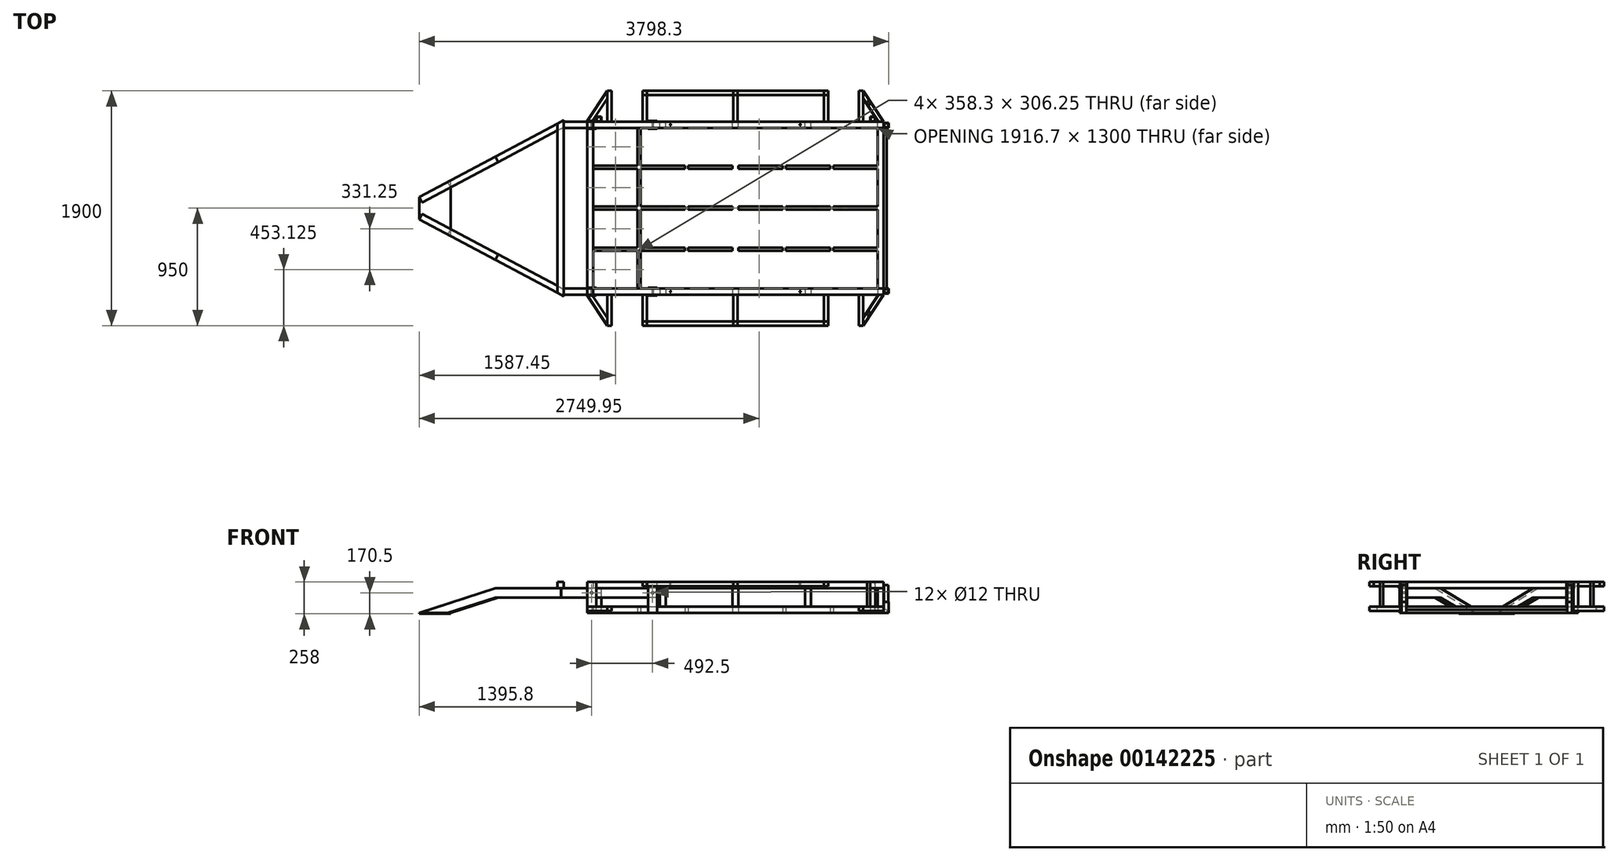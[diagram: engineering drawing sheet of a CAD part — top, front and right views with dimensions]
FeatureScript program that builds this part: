
annotation { "Feature Type Name" : "Feature", "Feature Type Description" : "" }
export const myFeature = defineFeature(function(context is Context, id is Id, definition is map)
    precondition{}
    {
        {
            var Q0;
            Q0=qCreatedBy(makeId("Top.planeOp"),FACE);
            var sketch = newSketch(context, id + "F0", { "sketchPlane" : qUnion([Q0])});
            skLineSegment(sketch, "E0.bottom", {"start": v(0, 700) * mm, "end": v(2400, 700) * mm});
            skLineSegment(sketch, "E0.top", {"start": v(0, -700) * mm, "end": v(2400, -700) * mm});
            skLineSegment(sketch, "E0.left", {"start": v(0, 700) * mm, "end": v(0, -700) * mm});
            skLineSegment(sketch, "E0.right", {"start": v(2400, 700) * mm, "end": v(2400, -700) * mm});
            skLineSegment(sketch, "E1.0", {"start": v(50, 650) * mm, "end": v(2350, 650) * mm});
            skLineSegment(sketch, "E2.0", {"start": v(50, -650) * mm, "end": v(2350, -650) * mm});
            skLineSegment(sketch, "E3.0", {"start": v(50, 650) * mm, "end": v(50, -650) * mm});
            skLineSegment(sketch, "E4", {"start": v(420.8, -898.2) * mm, "end": v(420.8, -1248.28) * mm, "construction": true});
            skLineSegment(sketch, "E5", {"start": v(804.2, -904.13) * mm, "end": v(804.2, -1242.34) * mm, "construction": true});
            skPoint(sketch, "E6.startSnap0", {"position": v(1200, -650) * mm});
            skLineSegment(sketch, "E7", {"start": v(1979.1, -862.6) * mm, "end": v(1979.1, -1218.6) * mm, "construction": true});
            skLineSegment(sketch, "E8", {"start": v(1595.8, -880.4) * mm, "end": v(1595.8, -1230.47) * mm, "construction": true});
            skLineSegment(sketch, "E9", {"start": v(1200, -876.97) * mm, "end": v(1200, -1568.23) * mm, "construction": true});
            skPoint(sketch, "E9.startSnap0", {"position": v(1200, -700) * mm});
            skLineSegment(sketch, "E10", {"start": v(408.3, 650) * mm, "end": v(408.3, -650) * mm});
            skLineSegment(sketch, "E11", {"start": v(791.7, -650) * mm, "end": v(791.7, 650) * mm});
            skLineSegment(sketch, "E12", {"start": v(1608.3, -650) * mm, "end": v(1608.3, 650) * mm});
            skLineSegment(sketch, "E13.0", {"start": v(1966.6, -650) * mm, "end": v(1966.6, 650) * mm});
            skLineSegment(sketch, "E14.0", {"start": v(1583.3, -650) * mm, "end": v(1583.3, 650) * mm});
            skLineSegment(sketch, "E15.0", {"start": v(816.7, -650) * mm, "end": v(816.7, 650) * mm});
            skLineSegment(sketch, "E16.0", {"start": v(433.3, 650) * mm, "end": v(433.3, -650) * mm});
            skLineSegment(sketch, "E17", {"start": v(-204.2, 331.25) * mm, "end": v(-574.65, 331.25) * mm, "construction": true});
            skLineSegment(sketch, "E18", {"start": v(-235.96, 0) * mm, "end": v(-549.96, 0) * mm});
            skLineSegment(sketch, "E19", {"start": v(-193.62, -331.25) * mm, "end": v(-624.05, -331.25) * mm, "construction": true});
            skLineSegment(sketch, "E20", {"start": v(50, 343.75) * mm, "end": v(408.3, 343.75) * mm});
            skLineSegment(sketch, "E21", {"start": v(50, -318.75) * mm, "end": v(408.3, -318.75) * mm});
            skLineSegment(sketch, "E22.0", {"start": v(50, 318.75) * mm, "end": v(408.3, 318.75) * mm});
            skLineSegment(sketch, "E23.0", {"start": v(50, -343.75) * mm, "end": v(408.3, -343.75) * mm});
            skLineSegment(sketch, "E24", {"start": v(50, 12.5) * mm, "end": v(408.3, 12.5) * mm});
            skLineSegment(sketch, "E25.0", {"start": v(50, -12.5) * mm, "end": v(408.3, -12.5) * mm});
            skLineSegment(sketch, "E26.trimOffspring", {"start": v(433.3, 343.75) * mm, "end": v(791.7, 343.75) * mm});
            skLineSegment(sketch, "E27.trimOffspring", {"start": v(433.3, 318.75) * mm, "end": v(791.7, 318.75) * mm});
            skLineSegment(sketch, "E28.trimOffspring", {"start": v(433.3, 12.5) * mm, "end": v(791.7, 12.5) * mm});
            skLineSegment(sketch, "E29.trimOffspring", {"start": v(433.3, -12.5) * mm, "end": v(791.7, -12.5) * mm});
            skLineSegment(sketch, "E30.trimOffspring", {"start": v(433.3, -318.75) * mm, "end": v(791.7, -318.75) * mm});
            skLineSegment(sketch, "E31.trimOffspring", {"start": v(433.3, -343.75) * mm, "end": v(791.7, -343.75) * mm});
            skLineSegment(sketch, "E32.trimOffspring", {"start": v(1608.3, -343.75) * mm, "end": v(1966.6, -343.75) * mm});
            skLineSegment(sketch, "E33.trimOffspring", {"start": v(1608.3, -318.75) * mm, "end": v(1966.6, -318.75) * mm});
            skLineSegment(sketch, "E34.trimOffspring", {"start": v(1608.3, -12.5) * mm, "end": v(1966.6, -12.5) * mm});
            skLineSegment(sketch, "E35.trimOffspring", {"start": v(1608.3, 12.5) * mm, "end": v(1966.6, 12.5) * mm});
            skLineSegment(sketch, "E36.trimOffspring", {"start": v(1608.3, 343.75) * mm, "end": v(1966.6, 343.75) * mm});
            skLineSegment(sketch, "E37.trimOffspring", {"start": v(1608.3, 318.75) * mm, "end": v(1966.6, 318.75) * mm});
            skLineSegment(sketch, "E38", {"start": v(1175, 650) * mm, "end": v(1175, -650) * mm});
            skLineSegment(sketch, "E39.0", {"start": v(1225, 650) * mm, "end": v(1225, -650) * mm});
            skLineSegment(sketch, "E40", {"start": v(1583.3, 343.75) * mm, "end": v(1225, 343.75) * mm});
            skLineSegment(sketch, "E41", {"start": v(1175, 343.75) * mm, "end": v(816.7, 343.75) * mm});
            skLineSegment(sketch, "E42", {"start": v(1175, 12.5) * mm, "end": v(816.7, 12.5) * mm});
            skLineSegment(sketch, "E43", {"start": v(1583.3, 12.5) * mm, "end": v(1225, 12.5) * mm});
            skLineSegment(sketch, "E44", {"start": v(1583.3, -318.75) * mm, "end": v(1225, -318.75) * mm});
            skLineSegment(sketch, "E45", {"start": v(1175, -318.75) * mm, "end": v(816.7, -318.75) * mm});
            skLineSegment(sketch, "E46.0", {"start": v(1175, 318.75) * mm, "end": v(816.7, 318.75) * mm});
            skLineSegment(sketch, "E47.0", {"start": v(1583.3, 318.75) * mm, "end": v(1225, 318.75) * mm});
            skLineSegment(sketch, "E48.0", {"start": v(1175, -12.5) * mm, "end": v(816.7, -12.5) * mm});
            skLineSegment(sketch, "E49.0", {"start": v(1583.3, -12.5) * mm, "end": v(1225, -12.5) * mm});
            skLineSegment(sketch, "E50.0", {"start": v(1175, -343.75) * mm, "end": v(816.7, -343.75) * mm});
            skLineSegment(sketch, "E51.0", {"start": v(1583.3, -343.75) * mm, "end": v(1225, -343.75) * mm});
            skLineSegment(sketch, "E52", {"start": v(816.7, 343.75) * mm, "end": v(816.7, 318.75) * mm});
            skLineSegment(sketch, "E53", {"start": v(1175, 343.75) * mm, "end": v(1175, 318.75) * mm});
            skLineSegment(sketch, "E54", {"start": v(1225, 343.75) * mm, "end": v(1225, 318.75) * mm});
            skLineSegment(sketch, "E55", {"start": v(1583.3, 343.75) * mm, "end": v(1583.3, 318.75) * mm});
            skLineSegment(sketch, "E56", {"start": v(1583.3, 12.5) * mm, "end": v(1583.3, -12.5) * mm});
            skLineSegment(sketch, "E57", {"start": v(1225, 12.5) * mm, "end": v(1225, -12.5) * mm});
            skLineSegment(sketch, "E58", {"start": v(1175, 12.5) * mm, "end": v(1175, -12.5) * mm});
            skLineSegment(sketch, "E59", {"start": v(816.7, 12.5) * mm, "end": v(816.7, -12.5) * mm});
            skLineSegment(sketch, "E60", {"start": v(1583.3, -318.75) * mm, "end": v(1583.3, -343.75) * mm});
            skLineSegment(sketch, "E61", {"start": v(1225, -318.75) * mm, "end": v(1225, -343.75) * mm});
            skLineSegment(sketch, "E62", {"start": v(1175, -318.75) * mm, "end": v(1175, -343.75) * mm});
            skLineSegment(sketch, "E63", {"start": v(816.7, -318.75) * mm, "end": v(816.7, -343.75) * mm});
            skLineSegment(sketch, "E64", {"start": v(2350, 650) * mm, "end": v(2350, -650) * mm});
            skLineSegment(sketch, "E65.0", {"start": v(1991.6, -650) * mm, "end": v(1991.6, 650) * mm});
            skLineSegment(sketch, "E66", {"start": v(1991.6, 343.75) * mm, "end": v(2350, 343.75) * mm});
            skLineSegment(sketch, "E67", {"start": v(1991.6, 12.5) * mm, "end": v(2350, 12.5) * mm});
            skLineSegment(sketch, "E68", {"start": v(1991.6, -318.75) * mm, "end": v(2350, -318.75) * mm});
            skLineSegment(sketch, "E69.0", {"start": v(1991.6, 318.75) * mm, "end": v(2350, 318.75) * mm});
            skLineSegment(sketch, "E70.0", {"start": v(1991.6, -12.5) * mm, "end": v(2350, -12.5) * mm});
            skLineSegment(sketch, "E71.0", {"start": v(1991.6, -343.75) * mm, "end": v(2350, -343.75) * mm});
            skLineSegment(sketch, "E72", {"start": v(1966.6, 650) * mm, "end": v(1991.6, 650) * mm});
            skLineSegment(sketch, "E73", {"start": v(1966.6, -650) * mm, "end": v(1991.6, -650) * mm});
            skLineSegment(sketch, "E74", {"start": v(1991.6, -343.75) * mm, "end": v(1991.6, -318.75) * mm});
            skLineSegment(sketch, "E75", {"start": v(2350, -343.75) * mm, "end": v(2350, -318.75) * mm});
            skLineSegment(sketch, "E76", {"start": v(2350, -12.5) * mm, "end": v(2350, 12.5) * mm});
            skLineSegment(sketch, "E77", {"start": v(1991.6, -12.5) * mm, "end": v(1991.6, 12.5) * mm});
            skLineSegment(sketch, "E78", {"start": v(2350, 318.75) * mm, "end": v(2350, 343.75) * mm});
            skLineSegment(sketch, "E79", {"start": v(1991.6, 318.75) * mm, "end": v(1991.6, 343.75) * mm});
            skLineSegment(sketch, "E80", {"start": v(2350, 343.75) * mm, "end": v(2350, 318.75) * mm});
            skLineSegment(sketch, "E81", {"start": v(2350, 12.5) * mm, "end": v(2350, -12.5) * mm});
            skLineSegment(sketch, "E82", {"start": v(2350, -318.75) * mm, "end": v(2350, -343.75) * mm});
            skLineSegment(sketch, "E83", {"start": v(1991.6, -318.75) * mm, "end": v(1991.6, -343.75) * mm});
            skLineSegment(sketch, "E84", {"start": v(1966.6, 343.75) * mm, "end": v(1966.6, 318.75) * mm});
            skLineSegment(sketch, "E85", {"start": v(1966.6, 12.5) * mm, "end": v(1966.6, -12.5) * mm});
            skLineSegment(sketch, "E86", {"start": v(1966.6, -318.75) * mm, "end": v(1966.6, -343.75) * mm});
            skLineSegment(sketch, "E87", {"start": v(1608.3, -318.75) * mm, "end": v(1608.3, -343.75) * mm});
            skLineSegment(sketch, "E88", {"start": v(1608.3, 12.5) * mm, "end": v(1608.3, -12.5) * mm});
            skLineSegment(sketch, "E89", {"start": v(1608.3, 343.75) * mm, "end": v(1608.3, 318.75) * mm});
            skSolve(sketch);
        }
        {
            var Q0;
            Q0=qSketchRegion(id+"F0",true);
            var Q1;
            Q1=makeQuery(id+"F0.imprint","IMPRINT",FACE,{"disambiguationData":[TD([[makeQuery(id+"F0.imprint","IMPRINT",EDGE,{"derivedFrom":sQuery(id+"F0.wireOp",EDGE,"E66")}),-1.0]])]});
            var Q2;
            {var subQ6=sQuery(id+"F0.wireOp",EDGE,"E72");Q2=makeQuery(id+"F0.imprint","IMPRINT",FACE,{"disambiguationData":[TD([[makeQuery(id+"F0.imprint","IMPRINT",EDGE,{"derivedFrom":subQ6}),-1.0]])]});}
            var Q3;
            Q3=makeQuery(id+"F0.imprint","IMPRINT",FACE,{"disambiguationData":[TD([[makeQuery(id+"F0.imprint","IMPRINT",EDGE,{"derivedFrom":sQuery(id+"F0.wireOp",EDGE,"E67")}),-1.0]])]});
            var Q4;
            Q4=makeQuery(id+"F0.imprint","IMPRINT",FACE,{"disambiguationData":[TD([[makeQuery(id+"F0.imprint","IMPRINT",EDGE,{"derivedFrom":sQuery(id+"F0.wireOp",EDGE,"E68")}),-1.0]])]});
            var Q5;
            {var subQ0=sQuery(id+"F0.wireOp",EDGE,"E32.trimOffspring");Q5=makeQuery(id+"F0.imprint","IMPRINT",FACE,{"disambiguationData":[TD([[makeQuery(id+"F0.imprint","IMPRINT",EDGE,{"derivedFrom":subQ0}),1.0]])]});}
            var Q6;
            {var subQ15=sQuery(id+"F0.wireOp",EDGE,"E55");Q6=makeQuery(id+"F0.imprint","IMPRINT",FACE,{"disambiguationData":[TD([[makeQuery(id+"F0.imprint","IMPRINT",EDGE,{"derivedFrom":subQ15}),1.0]])]});}
            var Q7;
            {var subQ0=sQuery(id+"F0.wireOp",EDGE,"E34.trimOffspring");Q7=makeQuery(id+"F0.imprint","IMPRINT",FACE,{"disambiguationData":[TD([[makeQuery(id+"F0.imprint","IMPRINT",EDGE,{"derivedFrom":subQ0}),1.0]])]});}
            var Q8;
            {var subQ0=sQuery(id+"F0.wireOp",EDGE,"E36.trimOffspring");Q8=makeQuery(id+"F0.imprint","IMPRINT",FACE,{"disambiguationData":[TD([[makeQuery(id+"F0.imprint","IMPRINT",EDGE,{"derivedFrom":subQ0}),-1.0]])]});}
            var Q9;
            {var subQ13=sQuery(id+"F0.wireOp",EDGE,"E53");Q9=makeQuery(id+"F0.imprint","IMPRINT",FACE,{"disambiguationData":[TD([[makeQuery(id+"F0.imprint","IMPRINT",EDGE,{"derivedFrom":subQ13}),1.0]])]});}
            var Q10;
            {var subQ16=sQuery(id+"F0.wireOp",EDGE,"E52");Q10=makeQuery(id+"F0.imprint","IMPRINT",FACE,{"disambiguationData":[TD([[makeQuery(id+"F0.imprint","IMPRINT",EDGE,{"derivedFrom":subQ16}),-1.0]])]});}
            var Q11;
            Q11=makeQuery(id+"F0.imprint","IMPRINT",FACE,{"disambiguationData":[TD([[makeQuery(id+"F0.imprint","IMPRINT",EDGE,{"derivedFrom":sQuery(id+"F0.wireOp",EDGE,"E45")}),1.0]])]});
            var Q12;
            Q12=makeQuery(id+"F0.imprint","IMPRINT",FACE,{"disambiguationData":[TD([[makeQuery(id+"F0.imprint","IMPRINT",EDGE,{"derivedFrom":sQuery(id+"F0.wireOp",EDGE,"E44")}),1.0]])]});
            var Q13;
            Q13=makeQuery(id+"F0.imprint","IMPRINT",FACE,{"disambiguationData":[TD([[makeQuery(id+"F0.imprint","IMPRINT",EDGE,{"derivedFrom":sQuery(id+"F0.wireOp",EDGE,"E43")}),1.0]])]});
            var Q14;
            Q14=makeQuery(id+"F0.imprint","IMPRINT",FACE,{"disambiguationData":[TD([[makeQuery(id+"F0.imprint","IMPRINT",EDGE,{"derivedFrom":sQuery(id+"F0.wireOp",EDGE,"E42")}),1.0]])]});
            var Q15;
            Q15=makeQuery(id+"F0.imprint","IMPRINT",FACE,{"disambiguationData":[TD([[makeQuery(id+"F0.imprint","IMPRINT",EDGE,{"derivedFrom":sQuery(id+"F0.wireOp",EDGE,"E40")}),1.0]])]});
            var Q16;
            Q16=makeQuery(id+"F0.imprint","IMPRINT",FACE,{"disambiguationData":[TD([[makeQuery(id+"F0.imprint","IMPRINT",EDGE,{"derivedFrom":sQuery(id+"F0.wireOp",EDGE,"E41")}),1.0]])]});
            var Q17;
            {var subQ0=sQuery(id+"F0.wireOp",EDGE,"E10");var subQ9=sQuery(id+"F0.wireOp",EDGE,"E1.0");var subQ10=makeQuery(id+"F0.imprint","INTERSECT",VERTEX,{"derivedFrom":[subQ9,subQ0]});Q17=makeQuery(id+"F0.imprint","IMPRINT",FACE,{"disambiguationData":[TD([[makeQuery(id+"F0.imprint","IMPRINT",EDGE,{"disambiguationData":[TD([[subQ10,-1.0]])],"derivedFrom":subQ9}),-1.0]])]});}
            var Q18;
            {var subQ0=sQuery(id+"F0.wireOp",EDGE,"E20");Q18=makeQuery(id+"F0.imprint","IMPRINT",FACE,{"disambiguationData":[TD([[makeQuery(id+"F0.imprint","IMPRINT",EDGE,{"derivedFrom":subQ0}),-1.0]])]});}
            var Q19;
            {var subQ0=sQuery(id+"F0.wireOp",EDGE,"E26.trimOffspring");Q19=makeQuery(id+"F0.imprint","IMPRINT",FACE,{"disambiguationData":[TD([[makeQuery(id+"F0.imprint","IMPRINT",EDGE,{"derivedFrom":subQ0}),-1.0]])]});}
            var Q20;
            {var subQ0=sQuery(id+"F0.wireOp",EDGE,"E24");Q20=makeQuery(id+"F0.imprint","IMPRINT",FACE,{"disambiguationData":[TD([[makeQuery(id+"F0.imprint","IMPRINT",EDGE,{"derivedFrom":subQ0}),-1.0]])]});}
            var Q21;
            {var subQ0=sQuery(id+"F0.wireOp",EDGE,"E28.trimOffspring");Q21=makeQuery(id+"F0.imprint","IMPRINT",FACE,{"disambiguationData":[TD([[makeQuery(id+"F0.imprint","IMPRINT",EDGE,{"derivedFrom":subQ0}),-1.0]])]});}
            var Q22;
            {var subQ0=sQuery(id+"F0.wireOp",EDGE,"E21");Q22=makeQuery(id+"F0.imprint","IMPRINT",FACE,{"disambiguationData":[TD([[makeQuery(id+"F0.imprint","IMPRINT",EDGE,{"derivedFrom":subQ0}),-1.0]])]});}
            var Q23;
            {var subQ0=sQuery(id+"F0.wireOp",EDGE,"E30.trimOffspring");Q23=makeQuery(id+"F0.imprint","IMPRINT",FACE,{"disambiguationData":[TD([[makeQuery(id+"F0.imprint","IMPRINT",EDGE,{"derivedFrom":subQ0}),-1.0]])]});}
            extrude(context, id + "F1", {"entities" : qUnion([Q0, Q1, Q2, Q3, Q4, Q5, Q6, Q7, Q8, Q9, Q10, Q11, Q12, Q13, Q14, Q15, Q16, Q17, Q18, Q19, Q20, Q21, Q22, Q23]), "depth" : 50 * mm});
        }
        {
            var Q0;
            Q0=makeQuery(id+"F1.opExtrude","CAP_FACE",FACE,{"disambiguationData":[OSD([sQuery(id+"F0.wireOp",EDGE,"E0.bottom"),sQuery(id+"F0.wireOp",EDGE,"E0.top"),sQuery(id+"F0.wireOp",EDGE,"E0.left"),sQuery(id+"F0.wireOp",EDGE,"E0.right"),sQuery(id+"F0.wireOp",EDGE,"E1.0"),sQuery(id+"F0.wireOp",EDGE,"E2.0"),sQuery(id+"F0.wireOp",EDGE,"E3.0"),sQuery(id+"F0.wireOp",EDGE,"f5f57e1a-51e7-4856-8c74-94098f8169a8.0")])],"isStart":false});
            cPlane(context, id + "F2", {"entities" : qUnion([Q0]), "cplaneType" : CPlaneType.OFFSET, "offset" : 0 * mm, "width" : 150 * mm, "height" : 150 * mm});
        }
        {
            var Q0;
            Q0=qCreatedBy(id+"F2.planeOp",FACE);
            var sketch = newSketch(context, id + "F3", { "sketchPlane" : qUnion([Q0])});
            skLineSegment(sketch, "E90.bottom", {"start": v(2350, -650) * mm, "end": v(2400, -650) * mm});
            skLineSegment(sketch, "E90.top", {"start": v(2350, -700) * mm, "end": v(2400, -700) * mm});
            skLineSegment(sketch, "E90.left", {"start": v(2350, -650) * mm, "end": v(2350, -700) * mm});
            skLineSegment(sketch, "E90.right", {"start": v(2400, -650) * mm, "end": v(2400, -700) * mm});
            skLineSegment(sketch, "E91.bottom", {"start": v(1175, -650) * mm, "end": v(1225, -650) * mm});
            skLineSegment(sketch, "E91.top", {"start": v(1175, -700) * mm, "end": v(1225, -700) * mm});
            skLineSegment(sketch, "E91.left", {"start": v(1175, -650) * mm, "end": v(1175, -700) * mm});
            skLineSegment(sketch, "E91.right", {"start": v(1225, -650) * mm, "end": v(1225, -700) * mm});
            skLineSegment(sketch, "E92.bottom", {"start": v(1762.5, -650) * mm, "end": v(1812.5, -650) * mm});
            skLineSegment(sketch, "E92.top", {"start": v(1762.5, -700) * mm, "end": v(1812.5, -700) * mm});
            skLineSegment(sketch, "E92.left", {"start": v(1762.5, -650) * mm, "end": v(1762.5, -700) * mm});
            skLineSegment(sketch, "E92.right", {"start": v(1812.5, -650) * mm, "end": v(1812.5, -700) * mm});
            skPoint(sketch, "E93.firstSnap0", {"position": v(1787.5, -650) * mm});
            skLineSegment(sketch, "E93.bottom", {"start": v(587.5, -650) * mm, "end": v(637.5, -650) * mm});
            skLineSegment(sketch, "E93.top", {"start": v(587.5, -700) * mm, "end": v(637.5, -700) * mm});
            skLineSegment(sketch, "E93.left", {"start": v(587.5, -650) * mm, "end": v(587.5, -700) * mm});
            skLineSegment(sketch, "E93.right", {"start": v(637.5, -650) * mm, "end": v(637.5, -700) * mm});
            skSolve(sketch);
        }
        {
            var Q0;
            Q0=makeQuery(id+"F3.imprint","IMPRINT",FACE,{"disambiguationData":[TD([[makeQuery(id+"F3.imprint","IMPRINT",EDGE,{"derivedFrom":sQuery(id+"F3.wireOp",EDGE,"E93.bottom")}),-1.0]])]});
            var Q1;
            Q1=makeQuery(id+"F3.imprint","IMPRINT",FACE,{"disambiguationData":[TD([[makeQuery(id+"F3.imprint","IMPRINT",EDGE,{"derivedFrom":sQuery(id+"F3.wireOp",EDGE,"E91.bottom")}),-1.0]])]});
            var Q2;
            Q2=makeQuery(id+"F3.imprint","IMPRINT",FACE,{"disambiguationData":[TD([[makeQuery(id+"F3.imprint","IMPRINT",EDGE,{"derivedFrom":sQuery(id+"F3.wireOp",EDGE,"E92.bottom")}),-1.0]])]});
            var Q3;
            Q3=makeQuery(id+"F3.imprint","IMPRINT",FACE,{"disambiguationData":[TD([[makeQuery(id+"F3.imprint","IMPRINT",EDGE,{"derivedFrom":sQuery(id+"F3.wireOp",EDGE,"E90.bottom")}),-1.0]])]});
            var Q4;
            Q4=sQuery(id+"F3.wireOp",EDGE,"E93.bottom");
            var Q5;
            Q5=sQuery(id+"F3.wireOp",EDGE,"E93.right");
            var Q6;
            Q6=sQuery(id+"F3.wireOp",EDGE,"E93.left");
            var Q7;
            Q7=sQuery(id+"F3.wireOp",EDGE,"E93.top");
            var Q8;
            Q8=sQuery(id+"F3.wireOp",EDGE,"E91.left");
            var Q9;
            Q9=sQuery(id+"F3.wireOp",EDGE,"E91.bottom");
            var Q10;
            Q10=sQuery(id+"F3.wireOp",EDGE,"E91.right");
            var Q11;
            Q11=sQuery(id+"F3.wireOp",EDGE,"E91.top");
            var Q12;
            Q12=sQuery(id+"F3.wireOp",EDGE,"E92.bottom");
            var Q13;
            Q13=sQuery(id+"F3.wireOp",EDGE,"E92.right");
            var Q14;
            Q14=sQuery(id+"F3.wireOp",EDGE,"E92.top");
            var Q15;
            Q15=sQuery(id+"F3.wireOp",EDGE,"E92.left");
            var Q16;
            Q16=sQuery(id+"F3.wireOp",EDGE,"E90.bottom");
            var Q17;
            Q17=sQuery(id+"F3.wireOp",EDGE,"E90.left");
            var Q18;
            Q18=sQuery(id+"F3.wireOp",EDGE,"E90.right");
            var Q19;
            Q19=sQuery(id+"F3.wireOp",EDGE,"E90.top");
            extrude(context, id + "F4", {"entities" : qUnion([Q0, Q1, Q2, Q3]), "surfaceEntities" : qUnion([Q4, Q5, Q6, Q7, Q8, Q9, Q10, Q11, Q12, Q13, Q14, Q15, Q16, Q17, Q18, Q19]), "depth" : 150 * mm});
        }
        {
            var Q0;
            Q0=qCreatedBy(makeId("Top.planeOp"),FACE);
            cPlane(context, id + "F5", {"entities" : qUnion([Q0]), "cplaneType" : CPlaneType.OFFSET, "offset" : 200 * mm, "width" : 150 * mm, "height" : 150 * mm});
        }
        {
            var Q0;
            Q0=qCreatedBy(id+"F5.planeOp",FACE);
            var sketch = newSketch(context, id + "F6", { "sketchPlane" : qUnion([Q0])});
            skLineSegment(sketch, "E94.0.0", {"start": v(2400, -650) * mm, "end": v(2350, -650) * mm});
            skLineSegment(sketch, "E94.0.1", {"start": v(2350, -650) * mm, "end": v(2350, -700) * mm});
            skLineSegment(sketch, "E94.0.2", {"start": v(2350, -700) * mm, "end": v(2400, -700) * mm});
            skLineSegment(sketch, "E94.0.3", {"start": v(2400, -700) * mm, "end": v(2400, -650) * mm});
            skLineSegment(sketch, "E95.bottom", {"start": v(2400, -650) * mm, "end": v(0, -650) * mm});
            skLineSegment(sketch, "E95.top", {"start": v(2400, -700) * mm, "end": v(0, -700) * mm});
            skLineSegment(sketch, "E95.left", {"start": v(2400, -650) * mm, "end": v(2400, -700) * mm});
            skLineSegment(sketch, "E95.right", {"start": v(0, -650) * mm, "end": v(0, -700) * mm});
            skSolve(sketch);
        }
        {
            var Q0;
            Q0=qSketchRegion(id+"F6",true);
            extrude(context, id + "F7", {"entities" : qUnion([Q0]), "depth" : 50 * mm});
        }
        {
            var Q0;
            Q0=qCreatedBy(makeId("Top.planeOp"),FACE);
            cPlane(context, id + "F8", {"entities" : qUnion([Q0]), "cplaneType" : CPlaneType.OFFSET, "offset" : 250 * mm, "width" : 150 * mm, "height" : 150 * mm});
        }
        {
            var Q0;
            Q0=qCreatedBy(id+"F8.planeOp",FACE);
            var sketch = newSketch(context, id + "F9", { "sketchPlane" : qUnion([Q0])});
            skLineSegment(sketch, "E96.bottom", {"start": v(0, -700) * mm, "end": v(75, -700) * mm});
            skLineSegment(sketch, "E96.top", {"start": v(0, -706) * mm, "end": v(75, -706) * mm});
            skLineSegment(sketch, "E96.left", {"start": v(0, -700) * mm, "end": v(0, -706) * mm});
            skLineSegment(sketch, "E96.right", {"start": v(75, -700) * mm, "end": v(75, -706) * mm});
            skLineSegment(sketch, "E97.bottom", {"start": v(0, -644) * mm, "end": v(75, -644) * mm});
            skLineSegment(sketch, "E97.top", {"start": v(0, -650) * mm, "end": v(75, -650) * mm});
            skLineSegment(sketch, "E97.left", {"start": v(0, -644) * mm, "end": v(0, -650) * mm});
            skLineSegment(sketch, "E97.right", {"start": v(75, -644) * mm, "end": v(75, -650) * mm});
            skLineSegment(sketch, "E98.bottom", {"start": v(567.5, -650) * mm, "end": v(492.5, -650) * mm});
            skLineSegment(sketch, "E98.top", {"start": v(567.5, -644) * mm, "end": v(492.5, -644) * mm});
            skLineSegment(sketch, "E98.left", {"start": v(567.5, -650) * mm, "end": v(567.5, -644) * mm});
            skLineSegment(sketch, "E98.right", {"start": v(492.5, -650) * mm, "end": v(492.5, -644) * mm});
            skLineSegment(sketch, "E99.bottom", {"start": v(567.5, -706) * mm, "end": v(492.5, -706) * mm});
            skLineSegment(sketch, "E99.top", {"start": v(567.5, -700) * mm, "end": v(492.5, -700) * mm});
            skLineSegment(sketch, "E99.left", {"start": v(567.5, -700) * mm, "end": v(567.5, -706) * mm});
            skLineSegment(sketch, "E99.right", {"start": v(492.5, -700) * mm, "end": v(492.5, -706) * mm});
            skLineSegment(sketch, "E100.0.0", {"start": v(587.5, -650) * mm, "end": v(587.5, -700) * mm});
            skLineSegment(sketch, "E100.0.2", {"start": v(587.5, -700) * mm, "end": v(587.5, -650) * mm});
            skSolve(sketch);
        }
        {
            var Q0;
            Q0=qSketchRegion(id+"F9",true);
            extrude(context, id + "F10", {"entities" : qUnion([Q0]), "oppositeDirection" : true, "depth" : 250 * mm});
        }
        {
            var Q0;
            Q0=qCreatedBy(makeId("Front.planeOp"),FACE);
            cPlane(context, id + "F11", {"entities" : qUnion([Q0]), "cplaneType" : CPlaneType.OFFSET, "offset" : 700 * mm, "width" : 150 * mm, "height" : 150 * mm});
        }
        {
            var Q0;
            Q0=qCreatedBy(id+"F11.planeOp",FACE);
            var sketch = newSketch(context, id + "F12", { "sketchPlane" : qUnion([Q0])});
            skLineSegment(sketch, "E101", {"start": v(1200, 250) * mm, "end": v(1200, 582.45) * mm, "construction": true});
            skLineSegment(sketch, "E102.bottom", {"start": v(1182.5, 250) * mm, "end": v(1217.5, 250) * mm});
            skLineSegment(sketch, "E102.top", {"start": v(1182.5, 215) * mm, "end": v(1217.5, 215) * mm});
            skLineSegment(sketch, "E102.left", {"start": v(1182.5, 250) * mm, "end": v(1182.5, 215) * mm});
            skLineSegment(sketch, "E102.right", {"start": v(1217.5, 250) * mm, "end": v(1217.5, 215) * mm});
            skLineSegment(sketch, "E103.bottom", {"start": v(450, 250) * mm, "end": v(485, 250) * mm});
            skLineSegment(sketch, "E103.top", {"start": v(450, 215) * mm, "end": v(485, 215) * mm});
            skLineSegment(sketch, "E103.left", {"start": v(450, 250) * mm, "end": v(450, 215) * mm});
            skLineSegment(sketch, "E103.right", {"start": v(485, 250) * mm, "end": v(485, 215) * mm});
            skLineSegment(sketch, "E104.MirrorCS", {"start": v(1950, 215) * mm, "end": v(1915, 215) * mm});
            skLineSegment(sketch, "E105.MirrorCS", {"start": v(1915, 250) * mm, "end": v(1915, 215) * mm});
            skLineSegment(sketch, "E106.MirrorCS", {"start": v(1950, 250) * mm, "end": v(1915, 250) * mm});
            skLineSegment(sketch, "E107.MirrorCS", {"start": v(1950, 250) * mm, "end": v(1950, 215) * mm});
            skLineSegment(sketch, "E108.bottom", {"start": v(165, 50) * mm, "end": v(200, 50) * mm});
            skLineSegment(sketch, "E108.top", {"start": v(165, 15) * mm, "end": v(200, 15) * mm});
            skLineSegment(sketch, "E108.left", {"start": v(200, 50) * mm, "end": v(200, 15) * mm});
            skLineSegment(sketch, "E108.right", {"start": v(165, 50) * mm, "end": v(165, 15) * mm});
            skLineSegment(sketch, "E109.bottom", {"start": v(2200, 50) * mm, "end": v(2235, 50) * mm});
            skLineSegment(sketch, "E109.top", {"start": v(2200, 15) * mm, "end": v(2235, 15) * mm});
            skLineSegment(sketch, "E109.left", {"start": v(2200, 50) * mm, "end": v(2200, 15) * mm});
            skLineSegment(sketch, "E109.right", {"start": v(2235, 50) * mm, "end": v(2235, 15) * mm});
            skSolve(sketch);
        }
        {
            var Q0;
            Q0=qSketchRegion(id+"F12",true);
            extrude(context, id + "F13", {"entities" : qUnion([Q0]), "depth" : 250 * mm});
        }
        {
            var Q0;
            Q0=qCreatedBy(makeId("Front.planeOp"),FACE);
            cPlane(context, id + "F14", {"entities" : qUnion([Q0]), "cplaneType" : CPlaneType.OFFSET, "offset" : 950 * mm, "width" : 150 * mm, "height" : 150 * mm});
        }
        {
            var Q0;
            Q0=qCreatedBy(id+"F14.planeOp",FACE);
            var sketch = newSketch(context, id + "F15", { "sketchPlane" : qUnion([Q0])});
            skLineSegment(sketch, "E110.bottom", {"start": v(1950, 250) * mm, "end": v(450, 250) * mm});
            skLineSegment(sketch, "E110.top", {"start": v(1950, 215) * mm, "end": v(450, 215) * mm});
            skLineSegment(sketch, "E110.left", {"start": v(1950, 250) * mm, "end": v(1950, 215) * mm});
            skLineSegment(sketch, "E110.right", {"start": v(450, 250) * mm, "end": v(450, 215) * mm});
            skSolve(sketch);
        }
        {
            var Q0;
            Q0=qSketchRegion(id+"F15",true);
            extrude(context, id + "F16", {"entities" : qUnion([Q0]), "oppositeDirection" : true, "depth" : 35 * mm});
        }
        {
            var Q0;
            Q0=qCreatedBy(id+"F2.planeOp",FACE);
            var sketch = newSketch(context, id + "F17", { "sketchPlane" : qUnion([Q0])});
            skLineSegment(sketch, "E111", {"start": v(0, -706) * mm, "end": v(165, -950) * mm});
            skLineSegment(sketch, "E112.0", {"start": v(42.25, -706) * mm, "end": v(165, -887.52) * mm});
            skLineSegment(sketch, "E113", {"start": v(2235, -950) * mm, "end": v(2400, -700) * mm});
            skLineSegment(sketch, "E114.0", {"start": v(2235, -886.46) * mm, "end": v(2358.06, -700) * mm});
            skLineSegment(sketch, "E115", {"start": v(165, -950) * mm, "end": v(165, -887.52) * mm});
            skLineSegment(sketch, "E116", {"start": v(0, -706) * mm, "end": v(42.25, -706) * mm});
            skLineSegment(sketch, "E117", {"start": v(2235, -886.46) * mm, "end": v(2235, -950) * mm});
            skLineSegment(sketch, "E118", {"start": v(2400, -700) * mm, "end": v(2358.06, -700) * mm});
            skSolve(sketch);
        }
        {
            var Q0;
            Q0=qSketchRegion(id+"F17",true);
            extrude(context, id + "F18", {"entities" : qUnion([Q0]), "oppositeDirection" : true, "depth" : 35 * mm});
        }
        {
            var Q0;
            Q0=qCreatedBy(id+"F8.planeOp",FACE);
            var sketch = newSketch(context, id + "F19", { "sketchPlane" : qUnion([Q0])});
            skLineSegment(sketch, "E119.bottom", {"start": v(75, -700) * mm, "end": v(115, -700) * mm});
            skLineSegment(sketch, "E119.top", {"start": v(75, -740) * mm, "end": v(115, -740) * mm});
            skLineSegment(sketch, "E119.left", {"start": v(75, -700) * mm, "end": v(75, -740) * mm});
            skLineSegment(sketch, "E119.right", {"start": v(115, -700) * mm, "end": v(115, -740) * mm});
            skLineSegment(sketch, "E120.bottom", {"start": v(2291.66, -700) * mm, "end": v(2331.66, -700) * mm});
            skLineSegment(sketch, "E120.top", {"start": v(2291.66, -740) * mm, "end": v(2331.66, -740) * mm});
            skLineSegment(sketch, "E120.left", {"start": v(2291.66, -700) * mm, "end": v(2291.66, -740) * mm});
            skLineSegment(sketch, "E120.right", {"start": v(2331.66, -700) * mm, "end": v(2331.66, -740) * mm});
            skLineSegment(sketch, "E121.bottom", {"start": v(77.5, -702.5) * mm, "end": v(112.5, -702.5) * mm});
            skLineSegment(sketch, "E121.top", {"start": v(77.5, -737.5) * mm, "end": v(112.5, -737.5) * mm});
            skLineSegment(sketch, "E121.left", {"start": v(77.5, -702.5) * mm, "end": v(77.5, -737.5) * mm});
            skLineSegment(sketch, "E121.right", {"start": v(112.5, -702.5) * mm, "end": v(112.5, -737.5) * mm});
            skLineSegment(sketch, "E122.bottom", {"start": v(2294.16, -702.5) * mm, "end": v(2329.16, -702.5) * mm});
            skLineSegment(sketch, "E122.top", {"start": v(2294.16, -737.5) * mm, "end": v(2329.16, -737.5) * mm});
            skLineSegment(sketch, "E122.left", {"start": v(2294.16, -702.5) * mm, "end": v(2294.16, -737.5) * mm});
            skLineSegment(sketch, "E122.right", {"start": v(2329.16, -702.5) * mm, "end": v(2329.16, -737.5) * mm});
            skSolve(sketch);
        }
        {
            var Q0;
            Q0=qSketchRegion(id+"F19",true);
            extrude(context, id + "F20", {"entities" : qUnion([Q0]), "oppositeDirection" : true, "depth" : 250 * mm});
        }
        {
            var Q0;
            Q0=qCreatedBy(id+"F5.planeOp",FACE);
            var sketch = newSketch(context, id + "F21", { "sketchPlane" : qUnion([Q0])});
            skLineSegment(sketch, "E123", {"start": v(0, 0) * mm, "end": v(-2022.09, 0) * mm, "construction": true});
            skLineSegment(sketch, "E124.left", {"start": v(587.5, -650) * mm, "end": v(587.5, -700) * mm, "construction": true});
            skLineSegment(sketch, "E125.0", {"start": v(587.5, -650) * mm, "end": v(587.5, -700) * mm});
            skLineSegment(sketch, "E126.0", {"start": v(-212.7, -700) * mm, "end": v(-742.46, -418.32) * mm});
            skLineSegment(sketch, "E127", {"start": v(-718.99, -374.17) * mm, "end": v(-200.22, -650) * mm});
            skLineSegment(sketch, "E128", {"start": v(-200.22, -650) * mm, "end": v(587.5, -650) * mm});
            skLineSegment(sketch, "E129", {"start": v(587.5, -700) * mm, "end": v(-212.7, -700) * mm});
            skLineSegment(sketch, "E130", {"start": v(-718.99, -374.17) * mm, "end": v(-742.46, -418.32) * mm});
            skSolve(sketch);
        }
        {
            var Q0;
            Q0=qSketchRegion(id+"F21",true);
            extrude(context, id + "F22", {"entities" : qUnion([Q0]), "oppositeDirection" : true, "depth" : 75 * mm});
        }
        {
            var Q0;
            Q0=makeQuery(id+"F22.opExtrude","SWEPT_BODY",BODY,{"disambiguationData":[OSD([sQuery(id+"F21.wireOp",EDGE,"E125.0"),sQuery(id+"F21.wireOp",EDGE,"E126.0"),sQuery(id+"F21.wireOp",EDGE,"nhGC0fzd-JeSJ-VvNC-nyvA-TV85BdcC3g7a"),sQuery(id+"F21.wireOp",EDGE,"E127"),sQuery(id+"F21.wireOp",EDGE,"E128"),sQuery(id+"F21.wireOp",EDGE,"E129")])]});
            var Q1;
            Q1=qCreatedBy(makeId("Front.planeOp"),FACE);
            mirror(context, id + "F23", {"entities" : qUnion([Q0]), "mirrorPlane" : qUnion([Q1])});
        }
        {
            var Q0;
            Q0=makeQuery(id+"F7.opExtrude","SWEPT_BODY",BODY,{"disambiguationData":[OSD([sQuery(id+"F6.wireOp",EDGE,"E95.bottom"),sQuery(id+"F6.wireOp",EDGE,"E95.top"),sQuery(id+"F6.wireOp",EDGE,"E95.left"),sQuery(id+"F6.wireOp",EDGE,"E95.right")])]});
            var Q1;
            Q1=makeQuery(id+"F10.opExtrude","SWEPT_BODY",BODY,{"disambiguationData":[OSD([sQuery(id+"F9.wireOp",EDGE,"E97.bottom"),sQuery(id+"F9.wireOp",EDGE,"E97.top"),sQuery(id+"F9.wireOp",EDGE,"E97.left"),sQuery(id+"F9.wireOp",EDGE,"E97.right")])]});
            var Q2;
            Q2=makeQuery(id+"F10.opExtrude","SWEPT_BODY",BODY,{"disambiguationData":[OSD([sQuery(id+"F9.wireOp",EDGE,"E96.bottom"),sQuery(id+"F9.wireOp",EDGE,"E96.top"),sQuery(id+"F9.wireOp",EDGE,"E96.left"),sQuery(id+"F9.wireOp",EDGE,"E96.right")])]});
            var Q3;
            Q3=makeQuery(id+"F18.opExtrude","SWEPT_BODY",BODY,{"disambiguationData":[OSD([sQuery(id+"F17.wireOp",EDGE,"E111"),sQuery(id+"F17.wireOp",EDGE,"E112.0"),sQuery(id+"F17.wireOp",EDGE,"E115"),sQuery(id+"F17.wireOp",EDGE,"E116")])]});
            var Q4;
            Q4=makeQuery(id+"F13.opExtrude","SWEPT_BODY",BODY,{"disambiguationData":[OSD([sQuery(id+"F12.wireOp",EDGE,"E108.bottom"),sQuery(id+"F12.wireOp",EDGE,"E108.top"),sQuery(id+"F12.wireOp",EDGE,"E108.left"),sQuery(id+"F12.wireOp",EDGE,"E108.right")])]});
            var Q5;
            Q5=makeQuery(id+"F10.opExtrude","SWEPT_BODY",BODY,{"disambiguationData":[OSD([sQuery(id+"F9.wireOp",EDGE,"E99.bottom"),sQuery(id+"F9.wireOp",EDGE,"E99.top"),sQuery(id+"F9.wireOp",EDGE,"E99.left"),sQuery(id+"F9.wireOp",EDGE,"E99.right")])]});
            var Q6;
            Q6=makeQuery(id+"F10.opExtrude","SWEPT_BODY",BODY,{"disambiguationData":[OSD([sQuery(id+"F9.wireOp",EDGE,"E98.bottom"),sQuery(id+"F9.wireOp",EDGE,"E98.top"),sQuery(id+"F9.wireOp",EDGE,"E98.left"),sQuery(id+"F9.wireOp",EDGE,"E98.right")])]});
            var Q7;
            Q7=makeQuery(id+"F13.opExtrude","SWEPT_BODY",BODY,{"disambiguationData":[OSD([sQuery(id+"F12.wireOp",EDGE,"E103.bottom"),sQuery(id+"F12.wireOp",EDGE,"E103.top"),sQuery(id+"F12.wireOp",EDGE,"E103.left"),sQuery(id+"F12.wireOp",EDGE,"E103.right")])]});
            var Q8;
            Q8=makeQuery(id+"F16.opExtrude","SWEPT_BODY",BODY,{"disambiguationData":[OSD([sQuery(id+"F15.wireOp",EDGE,"E110.bottom"),sQuery(id+"F15.wireOp",EDGE,"E110.top"),sQuery(id+"F15.wireOp",EDGE,"E110.left"),sQuery(id+"F15.wireOp",EDGE,"E110.right")])]});
            var Q9;
            Q9=makeQuery(id+"F13.opExtrude","SWEPT_BODY",BODY,{"disambiguationData":[OSD([sQuery(id+"F12.wireOp",EDGE,"E102.bottom"),sQuery(id+"F12.wireOp",EDGE,"E102.top"),sQuery(id+"F12.wireOp",EDGE,"E102.left"),sQuery(id+"F12.wireOp",EDGE,"E102.right")])]});
            var Q10;
            Q10=makeQuery(id+"F20.opExtrude","SWEPT_BODY",BODY,{"disambiguationData":[OSD([sQuery(id+"F19.wireOp",EDGE,"E119.bottom"),sQuery(id+"F19.wireOp",EDGE,"E119.top"),sQuery(id+"F19.wireOp",EDGE,"E119.left"),sQuery(id+"F19.wireOp",EDGE,"E119.right")])]});
            var Q11;
            Q11=makeQuery(id+"F18.opExtrude","SWEPT_BODY",BODY,{"disambiguationData":[OSD([sQuery(id+"F17.wireOp",EDGE,"E113"),sQuery(id+"F17.wireOp",EDGE,"E114.0"),sQuery(id+"F17.wireOp",EDGE,"E117"),sQuery(id+"F17.wireOp",EDGE,"E118")])]});
            var Q12;
            Q12=makeQuery(id+"F13.opExtrude","SWEPT_BODY",BODY,{"disambiguationData":[OSD([sQuery(id+"F12.wireOp",EDGE,"E109.bottom"),sQuery(id+"F12.wireOp",EDGE,"E109.top"),sQuery(id+"F12.wireOp",EDGE,"E109.left"),sQuery(id+"F12.wireOp",EDGE,"E109.right")])]});
            var Q13;
            Q13=makeQuery(id+"F20.opExtrude","SWEPT_BODY",BODY,{"disambiguationData":[OSD([sQuery(id+"F19.wireOp",EDGE,"E120.bottom"),sQuery(id+"F19.wireOp",EDGE,"E120.top"),sQuery(id+"F19.wireOp",EDGE,"E120.left"),sQuery(id+"F19.wireOp",EDGE,"E120.right")])]});
            var Q14;
            Q14=makeQuery(id+"F4.opExtrude","SWEPT_BODY",BODY,{"disambiguationData":[OSD([sQuery(id+"F3.wireOp",EDGE,"E90.bottom"),sQuery(id+"F3.wireOp",EDGE,"E90.top"),sQuery(id+"F3.wireOp",EDGE,"E90.left"),sQuery(id+"F3.wireOp",EDGE,"E90.right")])]});
            var Q15;
            Q15=makeQuery(id+"F4.opExtrude","SWEPT_BODY",BODY,{"disambiguationData":[OSD([sQuery(id+"F3.wireOp",EDGE,"E92.bottom"),sQuery(id+"F3.wireOp",EDGE,"E92.top"),sQuery(id+"F3.wireOp",EDGE,"E92.left"),sQuery(id+"F3.wireOp",EDGE,"E92.right")])]});
            var Q16;
            Q16=makeQuery(id+"F4.opExtrude","SWEPT_BODY",BODY,{"disambiguationData":[OSD([sQuery(id+"F3.wireOp",EDGE,"E91.bottom"),sQuery(id+"F3.wireOp",EDGE,"E91.top"),sQuery(id+"F3.wireOp",EDGE,"E91.left"),sQuery(id+"F3.wireOp",EDGE,"E91.right")])]});
            var Q17;
            Q17=makeQuery(id+"F4.opExtrude","SWEPT_BODY",BODY,{"disambiguationData":[OSD([sQuery(id+"F3.wireOp",EDGE,"E93.bottom"),sQuery(id+"F3.wireOp",EDGE,"E93.top"),sQuery(id+"F3.wireOp",EDGE,"E93.left"),sQuery(id+"F3.wireOp",EDGE,"E93.right")])]});
            var Q18;
            Q18=makeQuery(id+"F13.opExtrude","SWEPT_BODY",BODY,{"disambiguationData":[OSD([sQuery(id+"F12.wireOp",EDGE,"E104.MirrorCS"),sQuery(id+"F12.wireOp",EDGE,"E105.MirrorCS"),sQuery(id+"F12.wireOp",EDGE,"E106.MirrorCS"),sQuery(id+"F12.wireOp",EDGE,"E107.MirrorCS")])]});
            var Q19;
            Q19=qCreatedBy(makeId("Front.planeOp"),FACE);
            mirror(context, id + "F24", {"entities" : qUnion([Q0, Q1, Q2, Q3, Q4, Q5, Q6, Q7, Q8, Q9, Q10, Q11, Q12, Q13, Q14, Q15, Q16, Q17, Q18]), "mirrorPlane" : qUnion([Q19])});
        }
        {
            var Q0;
            Q0=qCreatedBy(makeId("Front.planeOp"),FACE);
            var sketch = newSketch(context, id + "F25", { "sketchPlane" : qUnion([Q0])});
            skLineSegment(sketch, "E131.bottom", {"start": v(0, 250) * mm, "end": v(50, 250) * mm});
            skLineSegment(sketch, "E131.top", {"start": v(0, 200) * mm, "end": v(50, 200) * mm});
            skLineSegment(sketch, "E131.left", {"start": v(0, 250) * mm, "end": v(0, 200) * mm});
            skLineSegment(sketch, "E131.right", {"start": v(50, 250) * mm, "end": v(50, 200) * mm});
            skSolve(sketch);
        }
        {
            var Q0;
            Q0=qSketchRegion(id+"F25",true);
            extrude(context, id + "F26", {"entities" : qUnion([Q0]), "endBound" : BoundingType.SYMMETRIC, "depth" : 1400 * mm});
        }
        {
            var Q0;
            Q0=qCreatedBy(id+"F5.planeOp",FACE);
            var sketch = newSketch(context, id + "F27", { "sketchPlane" : qUnion([Q0])});
            skLineSegment(sketch, "E132", {"start": v(-190, 712.06) * mm, "end": v(-190, -712.06) * mm});
            skLineSegment(sketch, "E133.0", {"start": v(-240, 685.48) * mm, "end": v(-240, -685.48) * mm});
            skLineSegment(sketch, "E134.0", {"start": v(-212.7, 700) * mm, "end": v(-212.7, 700) * mm});
            skLineSegment(sketch, "E135.0", {"start": v(-212.7, -700) * mm, "end": v(-212.7, -700) * mm});
            skLineSegment(sketch, "E136", {"start": v(-190, 712.06) * mm, "end": v(-240, 685.48) * mm});
            skLineSegment(sketch, "E137", {"start": v(-190, -712.06) * mm, "end": v(-240, -685.48) * mm});
            skSolve(sketch);
        }
        {
            var Q0;
            Q0=qSketchRegion(id+"F27",true);
            extrude(context, id + "F28", {"entities" : qUnion([Q0]), "depth" : 50 * mm});
        }
        {
            var Q0;
            Q0=qCreatedBy(makeId("Front.planeOp"),FACE);
            var sketch = newSketch(context, id + "F29", { "sketchPlane" : qUnion([Q0])});
            skCircle(sketch, "E138", {"center": v(37.5, 162.5) * mm, "radius": 6 * mm});
            skCircle(sketch, "E139", {"center": v(530, 162.5) * mm, "radius": 6 * mm});
            skSolve(sketch);
        }
        {
            var Q0;
            Q0=qSketchRegion(id+"F29",true);
            extrude(context, id + "F30", {"entities" : qUnion([Q0]), "operationType" : NewBodyOperationType.REMOVE, "endBound" : BoundingType.SYMMETRIC, "oppositeDirection" : true, "depth" : 1800 * mm});
        }
        {
            var Q0;
            Q0=qCreatedBy(id+"F8.planeOp",FACE);
            var sketch = newSketch(context, id + "F31", { "sketchPlane" : qUnion([Q0])});
            skCircle(sketch, "E140", {"center": v(675, 675) * mm, "radius": 4.5 * mm});
            skCircle(sketch, "E141", {"center": v(1725, 675) * mm, "radius": 4.5 * mm});
            skLineSegment(sketch, "E142", {"start": v(1200, -902.28) * mm, "end": v(1200, 1134.5) * mm, "construction": true});
            skLineSegment(sketch, "E143.0", {"start": v(2400, 700) * mm, "end": v(0, 700) * mm});
            skCircle(sketch, "E144", {"center": v(675, -675) * mm, "radius": 4.5 * mm});
            skCircle(sketch, "E145", {"center": v(1725, -675) * mm, "radius": 4.5 * mm});
            skSolve(sketch);
        }
        {
            var Q0;
            Q0=qSketchRegion(id+"F31",true);
            extrude(context, id + "F32", {"entities" : qUnion([Q0]), "operationType" : NewBodyOperationType.REMOVE, "oppositeDirection" : true, "depth" : 51 * mm});
        }
        {
            var Q0;
            Q0=qCreatedBy(makeId("Top.planeOp"),FACE);
            cPlane(context, id + "F33", {"entities" : qUnion([Q0]), "cplaneType" : CPlaneType.OFFSET, "offset" : 125 * mm, "width" : 150 * mm, "height" : 150 * mm});
        }
        {
            var Q0;
            Q0=qCreatedBy(id+"F33.planeOp",FACE);
            var sketch = newSketch(context, id + "F34", { "sketchPlane" : qUnion([Q0])});
            skLineSegment(sketch, "E146", {"start": v(-1102.18, -170.42) * mm, "end": v(-794.62, -333.95) * mm});
            skLineSegment(sketch, "E147", {"start": v(-794.62, -333.95) * mm, "end": v(-818.1, -378.1) * mm});
            skLineSegment(sketch, "E148", {"start": v(-818.1, -378.1) * mm, "end": v(-1121.7, -216.67) * mm});
            skLineSegment(sketch, "E149", {"start": v(-1121.7, -216.67) * mm, "end": v(-1102.18, -170.42) * mm});
            skLineSegment(sketch, "E150.MirrorCS", {"start": v(-818.1, 378.1) * mm, "end": v(-1121.7, 216.67) * mm});
            skLineSegment(sketch, "E151.MirrorCS", {"start": v(-1102.18, 170.42) * mm, "end": v(-794.62, 333.95) * mm});
            skLineSegment(sketch, "E152.MirrorCS", {"start": v(-794.62, 333.95) * mm, "end": v(-818.1, 378.1) * mm});
            skLineSegment(sketch, "E153.MirrorCS", {"start": v(-1121.7, 216.67) * mm, "end": v(-1102.18, 170.42) * mm});
            skSolve(sketch);
        }
        {
            var Q0;
            Q0=qCreatedBy(id+"F2.planeOp",FACE);
            var sketch = newSketch(context, id + "F35", { "sketchPlane" : qUnion([Q0])});
            skLineSegment(sketch, "E154", {"start": v(-948.62, 276.34) * mm, "end": v(-925.73, 231.89) * mm});
            skLineSegment(sketch, "E155.MirrorCS", {"start": v(-948.62, -276.34) * mm, "end": v(-925.73, -231.89) * mm});
            skLineSegment(sketch, "E156", {"start": v(0, 0) * mm, "end": v(-1745.24, 0) * mm});
            skLineSegment(sketch, "E157.0", {"start": v(0, 60) * mm, "end": v(-1745.24, 60) * mm});
            skLineSegment(sketch, "E158.0", {"start": v(0, -60) * mm, "end": v(-1745.24, -60) * mm});
            skLineSegment(sketch, "E159", {"start": v(-925.73, 231.89) * mm, "end": v(-1259.53, 60) * mm});
            skLineSegment(sketch, "E160", {"start": v(-925.73, -231.89) * mm, "end": v(-1260, -60) * mm});
            skLineSegment(sketch, "E161", {"start": v(-948.62, -276.34) * mm, "end": v(-1368.74, -60) * mm});
            skLineSegment(sketch, "E162", {"start": v(-948.62, 276.34) * mm, "end": v(-1368.74, 60) * mm});
            skLineSegment(sketch, "E163", {"start": v(-1368.74, 60) * mm, "end": v(-1259.53, 60) * mm});
            skLineSegment(sketch, "E164", {"start": v(-1368.74, -60) * mm, "end": v(-1260, -60) * mm});
            skLineSegment(sketch, "E165", {"start": v(-1368.74, 60) * mm, "end": v(-1368.74, -235.28) * mm, "construction": true});
            skLineSegment(sketch, "E166", {"start": v(-1108.74, 60) * mm, "end": v(-1108.74, -252.68) * mm, "construction": true});
            skLineSegment(sketch, "E167", {"start": v(-1259.53, 60) * mm, "end": v(-1368.74, 60) * mm});
            skLineSegment(sketch, "E168", {"start": v(-1260, -60) * mm, "end": v(-1368.74, -60) * mm});
            skSolve(sketch);
        }
        {
            var Q0;
            Q0=qSketchRegion(id+"F19",true);
            extrude(context, id + "F36", {"entities" : qUnion([Q0]), "operationType" : NewBodyOperationType.REMOVE, "oppositeDirection" : true, "depth" : 255 * mm});
        }
        {
            var Q0;
            Q0=qCreatedBy(id+"F2.planeOp",FACE);
            var sketch = newSketch(context, id + "F37", { "sketchPlane" : qUnion([Q0])});
            skLineSegment(sketch, "E169", {"start": v(2291.66, -531.72) * mm, "end": v(2291.66, -1326.9) * mm, "construction": true});
            skLineSegment(sketch, "E170.bottom", {"start": v(2291.66, -839.15) * mm, "end": v(2266.66, -839.15) * mm});
            skLineSegment(sketch, "E170.top", {"start": v(2291.66, -864.15) * mm, "end": v(2266.66, -864.15) * mm});
            skLineSegment(sketch, "E170.left", {"start": v(2291.66, -839.15) * mm, "end": v(2291.66, -864.15) * mm});
            skLineSegment(sketch, "E170.right", {"start": v(2266.66, -839.15) * mm, "end": v(2266.66, -864.15) * mm});
            skLineSegment(sketch, "E171.MirrorCS", {"start": v(2291.66, 864.15) * mm, "end": v(2266.66, 864.15) * mm});
            skLineSegment(sketch, "E172.MirrorCS", {"start": v(2266.66, 839.15) * mm, "end": v(2266.66, 864.15) * mm});
            skLineSegment(sketch, "E173.MirrorCS", {"start": v(2291.66, 839.15) * mm, "end": v(2266.66, 839.15) * mm});
            skLineSegment(sketch, "E174.MirrorCS", {"start": v(2291.66, 839.15) * mm, "end": v(2291.66, 864.15) * mm});
            skSolve(sketch);
        }
        {
            var Q0;
            Q0=qSketchRegion(id+"F37",true);
            extrude(context, id + "F38", {"entities" : qUnion([Q0]), "depth" : 200 * mm});
        }
        {
            var Q0;
            Q0=qCreatedBy(makeId("Right.planeOp"),FACE);
            cPlane(context, id + "F39", {"entities" : qUnion([Q0]), "cplaneType" : CPlaneType.OFFSET, "offset" : 2400 * mm, "width" : 150 * mm, "height" : 150 * mm});
        }
        {
            var Q0;
            Q0=qCreatedBy(id+"F39.planeOp",FACE);
            var sketch = newSketch(context, id + "F40", { "sketchPlane" : qUnion([Q0])});
            skLineSegment(sketch, "E175.bottom", {"start": v(-650, 25) * mm, "end": v(650, 25) * mm});
            skLineSegment(sketch, "E175.top", {"start": v(-650, 0) * mm, "end": v(650, 0) * mm});
            skLineSegment(sketch, "E175.left", {"start": v(-650, 25) * mm, "end": v(-650, 0) * mm});
            skLineSegment(sketch, "E175.right", {"start": v(650, 25) * mm, "end": v(650, 0) * mm});
            skSolve(sketch);
        }
        {
            var Q0;
            Q0=qSketchRegion(id+"F40",true);
            extrude(context, id + "F41", {"entities" : qUnion([Q0]), "operationType" : NewBodyOperationType.ADD, "depth" : 25 * mm});
        }
        {
            var Q0;
            Q0=qCreatedBy(makeId("Top.planeOp"),FACE);
            var sketch = newSketch(context, id + "F42", { "sketchPlane" : qUnion([Q0])});
            skLineSegment(sketch, "E176.bottom", {"start": v(2400, -650) * mm, "end": v(2440, -650) * mm});
            skLineSegment(sketch, "E176.top", {"start": v(2400, -690) * mm, "end": v(2440, -690) * mm});
            skLineSegment(sketch, "E176.left", {"start": v(2400, -650) * mm, "end": v(2400, -690) * mm});
            skLineSegment(sketch, "E176.right", {"start": v(2440, -650) * mm, "end": v(2440, -690) * mm});
            skLineSegment(sketch, "E177.bottom", {"start": v(2402, -652) * mm, "end": v(2438, -652) * mm});
            skLineSegment(sketch, "E177.top", {"start": v(2402, -688) * mm, "end": v(2438, -688) * mm});
            skLineSegment(sketch, "E177.left", {"start": v(2402, -652) * mm, "end": v(2402, -688) * mm});
            skLineSegment(sketch, "E177.right", {"start": v(2438, -652) * mm, "end": v(2438, -688) * mm});
            skLineSegment(sketch, "E178.MirrorCS", {"start": v(2400, 650) * mm, "end": v(2440, 650) * mm});
            skLineSegment(sketch, "E179.MirrorCS", {"start": v(2402, 652) * mm, "end": v(2438, 652) * mm});
            skLineSegment(sketch, "E180.MirrorCS", {"start": v(2440, 650) * mm, "end": v(2440, 690) * mm});
            skLineSegment(sketch, "E181.MirrorCS", {"start": v(2438, 652) * mm, "end": v(2438, 688) * mm});
            skLineSegment(sketch, "E182.MirrorCS", {"start": v(2402, 652) * mm, "end": v(2402, 688) * mm});
            skLineSegment(sketch, "E183.MirrorCS", {"start": v(2400, 650) * mm, "end": v(2400, 690) * mm});
            skLineSegment(sketch, "E184.MirrorCS", {"start": v(2400, 690) * mm, "end": v(2440, 690) * mm});
            skLineSegment(sketch, "E185.MirrorCS", {"start": v(2402, 688) * mm, "end": v(2438, 688) * mm});
            skSolve(sketch);
        }
        {
            var Q0;
            Q0=qSketchRegion(id+"F42",true);
            extrude(context, id + "F43", {"entities" : qUnion([Q0]), "depth" : 90 * mm});
        }
        {
            var Q0;
            Q0=qCreatedBy(makeId("Top.planeOp"),FACE);
            var sketch = newSketch(context, id + "F44", { "sketchPlane" : qUnion([Q0])});
            skLineSegment(sketch, "E186.bottom", {"start": v(2402, -652) * mm, "end": v(2438, -652) * mm});
            skLineSegment(sketch, "E186.top", {"start": v(2402, -688) * mm, "end": v(2438, -688) * mm});
            skLineSegment(sketch, "E186.left", {"start": v(2402, -652) * mm, "end": v(2402, -688) * mm});
            skLineSegment(sketch, "E186.right", {"start": v(2438, -652) * mm, "end": v(2438, -688) * mm});
            skLineSegment(sketch, "E187.bottom", {"start": v(2404.5, -654.5) * mm, "end": v(2435.5, -654.5) * mm});
            skLineSegment(sketch, "E187.top", {"start": v(2404.5, -685.5) * mm, "end": v(2435.5, -685.5) * mm});
            skLineSegment(sketch, "E187.left", {"start": v(2404.5, -654.5) * mm, "end": v(2404.5, -685.5) * mm});
            skLineSegment(sketch, "E187.right", {"start": v(2435.5, -654.5) * mm, "end": v(2435.5, -685.5) * mm});
            skLineSegment(sketch, "E188.MirrorCS", {"start": v(2402, 652) * mm, "end": v(2438, 652) * mm});
            skLineSegment(sketch, "E189.MirrorCS", {"start": v(2404.5, 654.5) * mm, "end": v(2435.5, 654.5) * mm});
            skLineSegment(sketch, "E190.MirrorCS", {"start": v(2438, 652) * mm, "end": v(2438, 688) * mm});
            skLineSegment(sketch, "E191.MirrorCS", {"start": v(2435.5, 654.5) * mm, "end": v(2435.5, 685.5) * mm});
            skLineSegment(sketch, "E192.MirrorCS", {"start": v(2404.5, 654.5) * mm, "end": v(2404.5, 685.5) * mm});
            skLineSegment(sketch, "E193.MirrorCS", {"start": v(2402, 652) * mm, "end": v(2402, 688) * mm});
            skLineSegment(sketch, "E194.MirrorCS", {"start": v(2404.5, 685.5) * mm, "end": v(2435.5, 685.5) * mm});
            skLineSegment(sketch, "E195.MirrorCS", {"start": v(2402, 688) * mm, "end": v(2438, 688) * mm});
            skSolve(sketch);
        }
        {
            var Q0;
            Q0=qSketchRegion(id+"F44",true);
            extrude(context, id + "F45", {"entities" : qUnion([Q0]), "depth" : 225 * mm});
        }
        {
            var Q0;
            Q0=makeQuery(id+"F22.opExtrude","SWEPT_FACE",FACE,{"disambiguationData":[OSD([sQuery(id+"F21.wireOp",EDGE,"E126.0")])]});
            cPlane(context, id + "F46", {"entities" : qUnion([Q0]), "cplaneType" : CPlaneType.OFFSET, "offset" : 0 * mm, "width" : 150 * mm, "height" : 150 * mm});
        }
        {
            var Q0;
            Q0=qCreatedBy(id+"F46.planeOp",FACE);
            var sketch = newSketch(context, id + "F47", { "sketchPlane" : qUnion([Q0])});
            skLineSegment(sketch, "E196", {"start": v(-372.24, 0) * mm, "end": v(-1732.1, 0) * mm, "construction": true});
            skLineSegment(sketch, "E197.0", {"start": v(-459.16, 125) * mm, "end": v(-459.16, 200) * mm});
            skLineSegment(sketch, "E198", {"start": v(-459.16, 125) * mm, "end": v(-895.1, 0) * mm});
            skLineSegment(sketch, "E199", {"start": v(-459.16, 200) * mm, "end": v(-1156.65, 0) * mm});
            skLineSegment(sketch, "E200", {"start": v(-895.1, 0) * mm, "end": v(-1156.65, 0) * mm});
            skSolve(sketch);
        }
        {
            var Q0;
            Q0 = qSketchRegion(id + "F47", true);
            extrude(context, id + "F48", {"entities" : qUnion([Q0]), "oppositeDirection" : true, "depth" : 50 * mm});
        }
        {
            var Q0;
            Q0=qCreatedBy(makeId("Front.planeOp"),FACE);
            var sketch = newSketch(context, id + "F49", { "sketchPlane" : qUnion([Q0])});
            skLineSegment(sketch, "E201", {"start": v(0, 0) * mm, "end": v(-1679.3, 0) * mm});
            skSolve(sketch);
        }
        {
            var Q0;
            Q0=makeQuery(id+"F48.opExtrude","SWEPT_BODY",BODY,{"disambiguationData":[OSD([sQuery(id+"F47.wireOp",EDGE,"E197.0"),sQuery(id+"F47.wireOp",EDGE,"E198"),sQuery(id+"F47.wireOp",EDGE,"E199"),sQuery(id+"F47.wireOp",EDGE,"E200")])]});
            var Q1;
            Q1=qCreatedBy(makeId("Front.planeOp"),FACE);
            mirror(context, id + "F50", {"operationType" : NewBodyOperationType.ADD, "entities" : qUnion([Q0]), "mirrorPlane" : qUnion([Q1])});
        }
        {
            var Q0;
            Q0=qCreatedBy(makeId("Top.planeOp"),FACE);
            var sketch = newSketch(context, id + "F51", { "sketchPlane" : qUnion([Q0])});
            skLineSegment(sketch, "E202", {"start": v(-1358.3, -90.87) * mm, "end": v(-1358.3, 90.87) * mm});
            skLineSegment(sketch, "E203", {"start": v(-1103.89, -226.14) * mm, "end": v(-1103.89, 226.14) * mm});
            skLineSegment(sketch, "E204", {"start": v(-1358.3, 90.87) * mm, "end": v(-1103.89, 226.14) * mm});
            skLineSegment(sketch, "E205", {"start": v(-1103.89, -226.14) * mm, "end": v(-1358.3, -90.87) * mm});
            skSolve(sketch);
        }
        {
            var Q0;
            Q0 = qSketchRegion(id + "F51", true);
            extrude(context, id + "F52", {"entities" : qUnion([Q0]), "oppositeDirection" : true, "depth" : 8 * mm});
        }
    });
